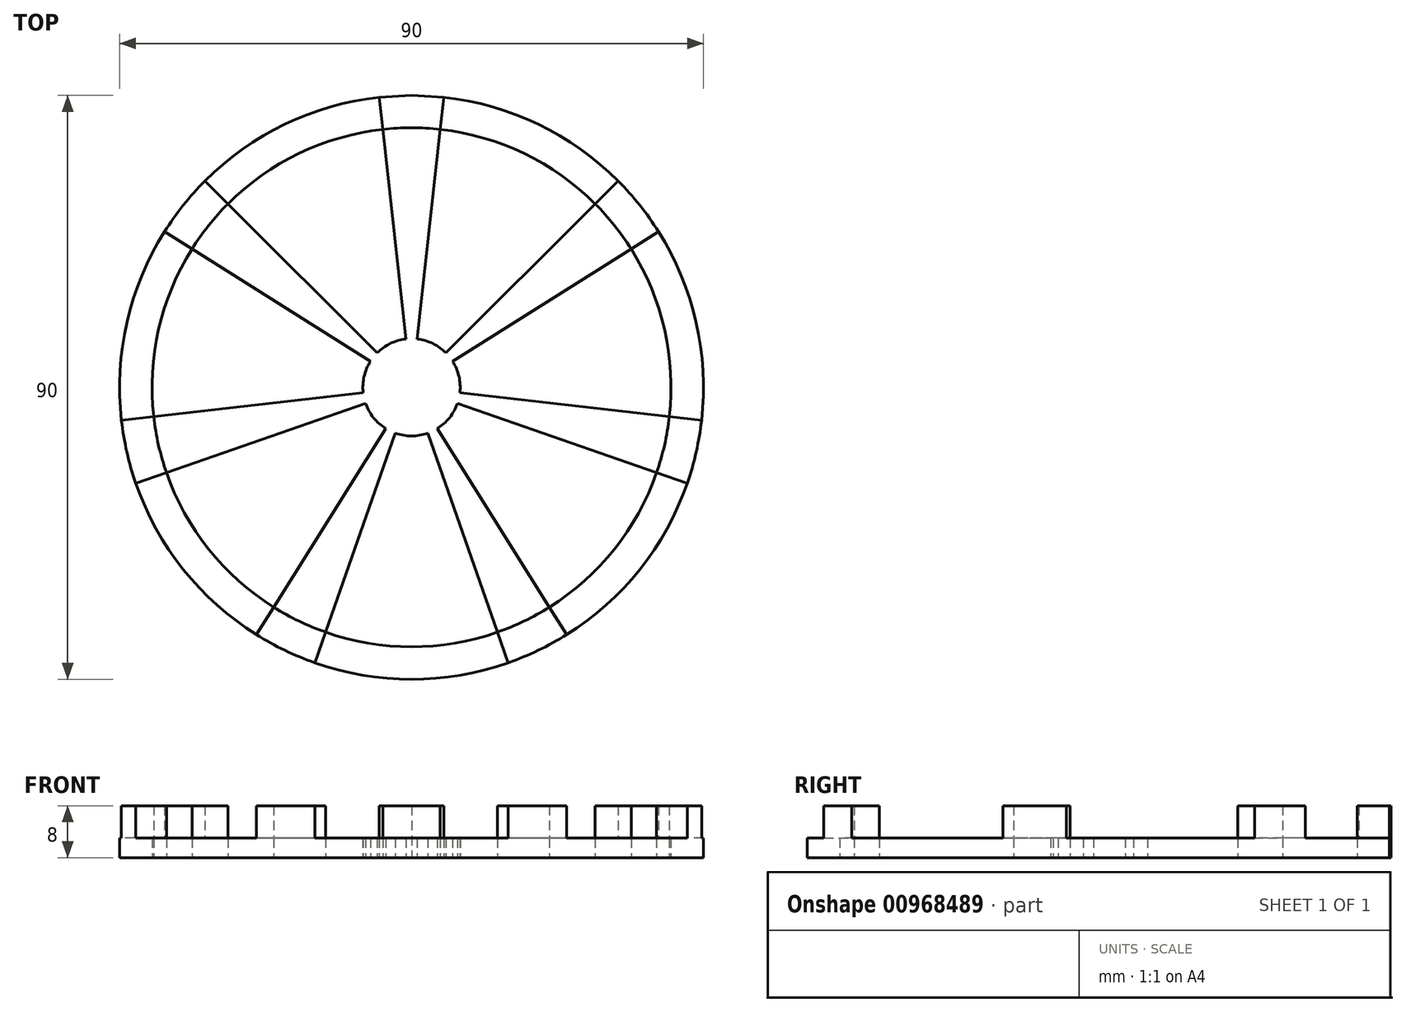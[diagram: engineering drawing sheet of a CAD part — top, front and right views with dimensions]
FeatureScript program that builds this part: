
annotation { "Feature Type Name" : "Feature", "Feature Type Description" : "" }
export const myFeature = defineFeature(function(context is Context, id is Id, definition is map)
    precondition{}
    {
        {
            var Q0;
            Q0=qCreatedBy(makeId("Top.planeOp"),FACE);
            var sketch = newSketch(context, id + "F0", { "sketchPlane" : qUnion([Q0])});
            skCircle(sketch, "E0", {"center": v(0, 0) * mm, "radius": 45 * mm});
            skCircle(sketch, "E1", {"center": v(0, 0) * mm, "radius": 7.5 * mm});
            skLineSegment(sketch, "E2", {"start": v(0, 45) * mm, "end": v(5, 44.72) * mm});
            skLineSegment(sketch, "E3.MirrorCS", {"start": v(0, 45) * mm, "end": v(-5, 44.72) * mm});
            skLineSegment(sketch, "E4", {"start": v(-5, 44.72) * mm, "end": v(0, 0) * mm});
            skLineSegment(sketch, "E5", {"start": v(0, 0) * mm, "end": v(5, 44.72) * mm});
            skLineSegment(sketch, "E6.1.0", {"start": v(0, 0) * mm, "end": v(-31.85, 31.79) * mm});
            skLineSegment(sketch, "E6.1.1", {"start": v(-38.08, 23.98) * mm, "end": v(0, 0) * mm});
            skLineSegment(sketch, "E6.2.0", {"start": v(0, 0) * mm, "end": v(-44.71, -5.08) * mm});
            skLineSegment(sketch, "E6.2.1", {"start": v(-42.5, -14.82) * mm, "end": v(0, 0) * mm});
            skLineSegment(sketch, "E6.3.0", {"start": v(0, 0) * mm, "end": v(-23.9, -38.13) * mm});
            skLineSegment(sketch, "E6.3.1", {"start": v(-14.9, -42.46) * mm, "end": v(0, 0) * mm});
            skLineSegment(sketch, "E6.4.0", {"start": v(0, 0) * mm, "end": v(14.9, -42.46) * mm});
            skLineSegment(sketch, "E6.4.1", {"start": v(23.9, -38.13) * mm, "end": v(0, 0) * mm});
            skLineSegment(sketch, "E6.5.0", {"start": v(0, 0) * mm, "end": v(42.5, -14.82) * mm});
            skLineSegment(sketch, "E6.5.1", {"start": v(44.71, -5.08) * mm, "end": v(0, 0) * mm});
            skLineSegment(sketch, "E6.6.0", {"start": v(0, 0) * mm, "end": v(38.08, 23.98) * mm});
            skLineSegment(sketch, "E6.6.1", {"start": v(31.85, 31.79) * mm, "end": v(0, 0) * mm});
            skPoint(sketch, "E7", {"position": v(-5.3, 5.3) * mm});
            skPoint(sketch, "E8", {"position": v(-0.83, 7.45) * mm});
            skPoint(sketch, "E9", {"position": v(0.83, 7.45) * mm});
            skPoint(sketch, "E10", {"position": v(5.3, 5.3) * mm});
            skPoint(sketch, "E11", {"position": v(6.35, 4) * mm});
            skPoint(sketch, "E12", {"position": v(7.45, -0.85) * mm});
            skPoint(sketch, "E13", {"position": v(7.08, -2.47) * mm});
            skPoint(sketch, "E14", {"position": v(3.98, -6.35) * mm});
            skPoint(sketch, "E15", {"position": v(2.48, -7.08) * mm});
            skPoint(sketch, "E16", {"position": v(-2.48, -7.08) * mm});
            skPoint(sketch, "E17", {"position": v(-3.98, -6.35) * mm});
            skPoint(sketch, "E18", {"position": v(-7.08, -2.47) * mm});
            skPoint(sketch, "E19", {"position": v(-7.45, -0.85) * mm});
            skPoint(sketch, "E20", {"position": v(-6.35, 4) * mm});
            skCircle(sketch, "E21.0", {"center": v(0, 0) * mm, "radius": 40 * mm});
            skSolve(sketch);
        }
        {
            var Q0;
            {var subQ1=sQuery(id+"F0.wireOp",EDGE,"E0");var subQ3=sQuery(id+"F0.wireOp",EDGE,"E6.1.0");var subQ4=makeQuery(id+"F0.imprint","INTERSECT",VERTEX,{"derivedFrom":[subQ1,subQ3]});Q0=makeQuery(id+"F0.imprint","IMPRINT",FACE,{"disambiguationData":[TD([[makeQuery(id+"F0.imprint","IMPRINT",EDGE,{"disambiguationData":[TD([[subQ4,1.0]])],"derivedFrom":subQ3}),-1.0]])]});}
            var Q1;
            {var subQ0=sQuery(id+"F0.wireOp",EDGE,"E6.1.0");var subQ1=sQuery(id+"F0.wireOp",EDGE,"E0");var subQ2=makeQuery(id+"F0.imprint","INTERSECT",VERTEX,{"derivedFrom":[subQ1,subQ0]});Q1=makeQuery(id+"F0.imprint","IMPRINT",FACE,{"disambiguationData":[TD([[makeQuery(id+"F0.imprint","IMPRINT",EDGE,{"disambiguationData":[TD([[subQ2,-1.0]])],"derivedFrom":subQ1}),1.0]])]});}
            var Q2;
            {var subQ0=sQuery(id+"F0.wireOp",EDGE,"E6.1.0");var subQ1=sQuery(id+"F0.wireOp",EDGE,"E1");var subQ2=makeQuery(id+"F0.imprint","INTERSECT",VERTEX,{"derivedFrom":[subQ1,subQ0]});Q2=makeQuery(id+"F0.imprint","IMPRINT",FACE,{"disambiguationData":[TD([[makeQuery(id+"F0.imprint","IMPRINT",EDGE,{"disambiguationData":[TD([[subQ2,-1.0]])],"derivedFrom":subQ1}),-1.0]])]});}
            var Q3;
            {var subQ0=sQuery(id+"F0.wireOp",EDGE,"E6.2.0");var subQ1=sQuery(id+"F0.wireOp",EDGE,"E1");var subQ2=makeQuery(id+"F0.imprint","INTERSECT",VERTEX,{"derivedFrom":[subQ1,subQ0]});Q3=makeQuery(id+"F0.imprint","IMPRINT",FACE,{"disambiguationData":[TD([[makeQuery(id+"F0.imprint","IMPRINT",EDGE,{"disambiguationData":[TD([[subQ2,-1.0]])],"derivedFrom":subQ1}),-1.0]])]});}
            var Q4;
            {var subQ0=sQuery(id+"F0.wireOp",EDGE,"E6.2.0");var subQ1=sQuery(id+"F0.wireOp",EDGE,"E0");var subQ2=makeQuery(id+"F0.imprint","INTERSECT",VERTEX,{"derivedFrom":[subQ1,subQ0]});Q4=makeQuery(id+"F0.imprint","IMPRINT",FACE,{"disambiguationData":[TD([[makeQuery(id+"F0.imprint","IMPRINT",EDGE,{"disambiguationData":[TD([[subQ2,-1.0]])],"derivedFrom":subQ1}),1.0]])]});}
            var Q5;
            {var subQ0=sQuery(id+"F0.wireOp",EDGE,"E6.1.1");var subQ1=sQuery(id+"F0.wireOp",EDGE,"E0");var subQ2=makeQuery(id+"F0.imprint","INTERSECT",VERTEX,{"derivedFrom":[subQ1,subQ0]});Q5=makeQuery(id+"F0.imprint","IMPRINT",FACE,{"disambiguationData":[TD([[makeQuery(id+"F0.imprint","IMPRINT",EDGE,{"disambiguationData":[TD([[subQ2,-1.0]])],"derivedFrom":subQ1}),1.0]])]});}
            var Q6;
            {var subQ0=sQuery(id+"F0.wireOp",EDGE,"E6.2.1");var subQ1=sQuery(id+"F0.wireOp",EDGE,"E0");var subQ2=makeQuery(id+"F0.imprint","INTERSECT",VERTEX,{"derivedFrom":[subQ1,subQ0]});Q6=makeQuery(id+"F0.imprint","IMPRINT",FACE,{"disambiguationData":[TD([[makeQuery(id+"F0.imprint","IMPRINT",EDGE,{"disambiguationData":[TD([[subQ2,-1.0]])],"derivedFrom":subQ1}),1.0]])]});}
            var Q7;
            {var subQ0=sQuery(id+"F0.wireOp",EDGE,"E6.3.0");var subQ1=sQuery(id+"F0.wireOp",EDGE,"E1");var subQ2=makeQuery(id+"F0.imprint","INTERSECT",VERTEX,{"derivedFrom":[subQ1,subQ0]});Q7=makeQuery(id+"F0.imprint","IMPRINT",FACE,{"disambiguationData":[TD([[makeQuery(id+"F0.imprint","IMPRINT",EDGE,{"disambiguationData":[TD([[subQ2,-1.0]])],"derivedFrom":subQ1}),-1.0]])]});}
            var Q8;
            {var subQ0=sQuery(id+"F0.wireOp",EDGE,"E6.3.0");var subQ1=sQuery(id+"F0.wireOp",EDGE,"E0");var subQ2=makeQuery(id+"F0.imprint","INTERSECT",VERTEX,{"derivedFrom":[subQ1,subQ0]});Q8=makeQuery(id+"F0.imprint","IMPRINT",FACE,{"disambiguationData":[TD([[makeQuery(id+"F0.imprint","IMPRINT",EDGE,{"disambiguationData":[TD([[subQ2,-1.0]])],"derivedFrom":subQ1}),1.0]])]});}
            var Q9;
            {var subQ0=sQuery(id+"F0.wireOp",EDGE,"E6.3.1");var subQ1=sQuery(id+"F0.wireOp",EDGE,"E0");var subQ2=makeQuery(id+"F0.imprint","INTERSECT",VERTEX,{"derivedFrom":[subQ1,subQ0]});Q9=makeQuery(id+"F0.imprint","IMPRINT",FACE,{"disambiguationData":[TD([[makeQuery(id+"F0.imprint","IMPRINT",EDGE,{"disambiguationData":[TD([[subQ2,-1.0]])],"derivedFrom":subQ1}),1.0]])]});}
            var Q10;
            {var subQ0=sQuery(id+"F0.wireOp",EDGE,"E6.4.0");var subQ1=sQuery(id+"F0.wireOp",EDGE,"E0");var subQ2=makeQuery(id+"F0.imprint","INTERSECT",VERTEX,{"derivedFrom":[subQ1,subQ0]});Q10=makeQuery(id+"F0.imprint","IMPRINT",FACE,{"disambiguationData":[TD([[makeQuery(id+"F0.imprint","IMPRINT",EDGE,{"disambiguationData":[TD([[subQ2,-1.0]])],"derivedFrom":subQ1}),1.0]])]});}
            var Q11;
            {var subQ0=sQuery(id+"F0.wireOp",EDGE,"E6.4.0");var subQ1=sQuery(id+"F0.wireOp",EDGE,"E1");var subQ2=makeQuery(id+"F0.imprint","INTERSECT",VERTEX,{"derivedFrom":[subQ1,subQ0]});Q11=makeQuery(id+"F0.imprint","IMPRINT",FACE,{"disambiguationData":[TD([[makeQuery(id+"F0.imprint","IMPRINT",EDGE,{"disambiguationData":[TD([[subQ2,-1.0]])],"derivedFrom":subQ1}),-1.0]])]});}
            var Q12;
            {var subQ0=sQuery(id+"F0.wireOp",EDGE,"E6.4.1");var subQ1=sQuery(id+"F0.wireOp",EDGE,"E0");var subQ2=makeQuery(id+"F0.imprint","INTERSECT",VERTEX,{"derivedFrom":[subQ1,subQ0]});Q12=makeQuery(id+"F0.imprint","IMPRINT",FACE,{"disambiguationData":[TD([[makeQuery(id+"F0.imprint","IMPRINT",EDGE,{"disambiguationData":[TD([[subQ2,-1.0]])],"derivedFrom":subQ1}),1.0]])]});}
            var Q13;
            {var subQ0=sQuery(id+"F0.wireOp",EDGE,"E6.5.0");var subQ1=sQuery(id+"F0.wireOp",EDGE,"E0");var subQ2=makeQuery(id+"F0.imprint","INTERSECT",VERTEX,{"derivedFrom":[subQ1,subQ0]});Q13=makeQuery(id+"F0.imprint","IMPRINT",FACE,{"disambiguationData":[TD([[makeQuery(id+"F0.imprint","IMPRINT",EDGE,{"disambiguationData":[TD([[subQ2,-1.0]])],"derivedFrom":subQ1}),1.0]])]});}
            var Q14;
            {var subQ0=sQuery(id+"F0.wireOp",EDGE,"E6.5.0");var subQ1=sQuery(id+"F0.wireOp",EDGE,"E1");var subQ2=makeQuery(id+"F0.imprint","INTERSECT",VERTEX,{"derivedFrom":[subQ1,subQ0]});Q14=makeQuery(id+"F0.imprint","IMPRINT",FACE,{"disambiguationData":[TD([[makeQuery(id+"F0.imprint","IMPRINT",EDGE,{"disambiguationData":[TD([[subQ2,-1.0]])],"derivedFrom":subQ1}),-1.0]])]});}
            var Q15;
            {var subQ0=sQuery(id+"F0.wireOp",EDGE,"E4");var subQ1=sQuery(id+"F0.wireOp",EDGE,"E1");var subQ2=makeQuery(id+"F0.imprint","INTERSECT",VERTEX,{"derivedFrom":[subQ1,subQ0]});Q15=makeQuery(id+"F0.imprint","IMPRINT",FACE,{"disambiguationData":[TD([[makeQuery(id+"F0.imprint","IMPRINT",EDGE,{"disambiguationData":[TD([[subQ2,-1.0]])],"derivedFrom":subQ1}),1.0]])]});}
            var Q16;
            {var subQ0=sQuery(id+"F0.wireOp",EDGE,"E6.1.0");var subQ1=sQuery(id+"F0.wireOp",EDGE,"E1");var subQ2=makeQuery(id+"F0.imprint","INTERSECT",VERTEX,{"derivedFrom":[subQ1,subQ0]});Q16=makeQuery(id+"F0.imprint","IMPRINT",FACE,{"disambiguationData":[TD([[makeQuery(id+"F0.imprint","IMPRINT",EDGE,{"disambiguationData":[TD([[subQ2,-1.0]])],"derivedFrom":subQ1}),1.0]])]});}
            var Q17;
            {var subQ0=sQuery(id+"F0.wireOp",EDGE,"E6.1.1");var subQ1=sQuery(id+"F0.wireOp",EDGE,"E1");var subQ2=makeQuery(id+"F0.imprint","INTERSECT",VERTEX,{"derivedFrom":[subQ1,subQ0]});Q17=makeQuery(id+"F0.imprint","IMPRINT",FACE,{"disambiguationData":[TD([[makeQuery(id+"F0.imprint","IMPRINT",EDGE,{"disambiguationData":[TD([[subQ2,-1.0]])],"derivedFrom":subQ1}),1.0]])]});}
            var Q18;
            {var subQ0=sQuery(id+"F0.wireOp",EDGE,"E6.2.0");var subQ1=sQuery(id+"F0.wireOp",EDGE,"E1");var subQ2=makeQuery(id+"F0.imprint","INTERSECT",VERTEX,{"derivedFrom":[subQ1,subQ0]});Q18=makeQuery(id+"F0.imprint","IMPRINT",FACE,{"disambiguationData":[TD([[makeQuery(id+"F0.imprint","IMPRINT",EDGE,{"disambiguationData":[TD([[subQ2,-1.0]])],"derivedFrom":subQ1}),1.0]])]});}
            var Q19;
            {var subQ0=sQuery(id+"F0.wireOp",EDGE,"E6.2.1");var subQ1=sQuery(id+"F0.wireOp",EDGE,"E1");var subQ2=makeQuery(id+"F0.imprint","INTERSECT",VERTEX,{"derivedFrom":[subQ1,subQ0]});Q19=makeQuery(id+"F0.imprint","IMPRINT",FACE,{"disambiguationData":[TD([[makeQuery(id+"F0.imprint","IMPRINT",EDGE,{"disambiguationData":[TD([[subQ2,-1.0]])],"derivedFrom":subQ1}),1.0]])]});}
            var Q20;
            {var subQ0=sQuery(id+"F0.wireOp",EDGE,"E6.3.0");var subQ1=sQuery(id+"F0.wireOp",EDGE,"E1");var subQ2=makeQuery(id+"F0.imprint","INTERSECT",VERTEX,{"derivedFrom":[subQ1,subQ0]});Q20=makeQuery(id+"F0.imprint","IMPRINT",FACE,{"disambiguationData":[TD([[makeQuery(id+"F0.imprint","IMPRINT",EDGE,{"disambiguationData":[TD([[subQ2,-1.0]])],"derivedFrom":subQ1}),1.0]])]});}
            var Q21;
            {var subQ0=sQuery(id+"F0.wireOp",EDGE,"E6.3.1");var subQ1=sQuery(id+"F0.wireOp",EDGE,"E1");var subQ2=makeQuery(id+"F0.imprint","INTERSECT",VERTEX,{"derivedFrom":[subQ1,subQ0]});Q21=makeQuery(id+"F0.imprint","IMPRINT",FACE,{"disambiguationData":[TD([[makeQuery(id+"F0.imprint","IMPRINT",EDGE,{"disambiguationData":[TD([[subQ2,-1.0]])],"derivedFrom":subQ1}),1.0]])]});}
            var Q22;
            {var subQ0=sQuery(id+"F0.wireOp",EDGE,"E6.4.0");var subQ1=sQuery(id+"F0.wireOp",EDGE,"E1");var subQ2=makeQuery(id+"F0.imprint","INTERSECT",VERTEX,{"derivedFrom":[subQ1,subQ0]});Q22=makeQuery(id+"F0.imprint","IMPRINT",FACE,{"disambiguationData":[TD([[makeQuery(id+"F0.imprint","IMPRINT",EDGE,{"disambiguationData":[TD([[subQ2,-1.0]])],"derivedFrom":subQ1}),1.0]])]});}
            var Q23;
            {var subQ0=sQuery(id+"F0.wireOp",EDGE,"E6.4.1");var subQ1=sQuery(id+"F0.wireOp",EDGE,"E1");var subQ2=makeQuery(id+"F0.imprint","INTERSECT",VERTEX,{"derivedFrom":[subQ1,subQ0]});Q23=makeQuery(id+"F0.imprint","IMPRINT",FACE,{"disambiguationData":[TD([[makeQuery(id+"F0.imprint","IMPRINT",EDGE,{"disambiguationData":[TD([[subQ2,-1.0]])],"derivedFrom":subQ1}),1.0]])]});}
            var Q24;
            {var subQ0=sQuery(id+"F0.wireOp",EDGE,"E6.5.0");var subQ1=sQuery(id+"F0.wireOp",EDGE,"E1");var subQ2=makeQuery(id+"F0.imprint","INTERSECT",VERTEX,{"derivedFrom":[subQ1,subQ0]});Q24=makeQuery(id+"F0.imprint","IMPRINT",FACE,{"disambiguationData":[TD([[makeQuery(id+"F0.imprint","IMPRINT",EDGE,{"disambiguationData":[TD([[subQ2,-1.0]])],"derivedFrom":subQ1}),1.0]])]});}
            var Q25;
            {var subQ0=sQuery(id+"F0.wireOp",EDGE,"E6.6.0");var subQ1=sQuery(id+"F0.wireOp",EDGE,"E1");var subQ2=makeQuery(id+"F0.imprint","INTERSECT",VERTEX,{"derivedFrom":[subQ1,subQ0]});Q25=makeQuery(id+"F0.imprint","IMPRINT",FACE,{"disambiguationData":[TD([[makeQuery(id+"F0.imprint","IMPRINT",EDGE,{"disambiguationData":[TD([[subQ2,1.0]])],"derivedFrom":subQ1}),1.0]])]});}
            var Q26;
            {var subQ0=sQuery(id+"F0.wireOp",EDGE,"E6.6.1");var subQ1=sQuery(id+"F0.wireOp",EDGE,"E1");var subQ2=makeQuery(id+"F0.imprint","INTERSECT",VERTEX,{"derivedFrom":[subQ1,subQ0]});Q26=makeQuery(id+"F0.imprint","IMPRINT",FACE,{"disambiguationData":[TD([[makeQuery(id+"F0.imprint","IMPRINT",EDGE,{"disambiguationData":[TD([[subQ2,1.0]])],"derivedFrom":subQ1}),1.0]])]});}
            var Q27;
            {var subQ0=sQuery(id+"F0.wireOp",EDGE,"E6.6.1");var subQ1=sQuery(id+"F0.wireOp",EDGE,"E1");var subQ2=makeQuery(id+"F0.imprint","INTERSECT",VERTEX,{"derivedFrom":[subQ1,subQ0]});Q27=makeQuery(id+"F0.imprint","IMPRINT",FACE,{"disambiguationData":[TD([[makeQuery(id+"F0.imprint","IMPRINT",EDGE,{"disambiguationData":[TD([[subQ2,-1.0]])],"derivedFrom":subQ1}),1.0]])]});}
            var Q28;
            {var subQ0=sQuery(id+"F0.wireOp",EDGE,"E5");var subQ1=sQuery(id+"F0.wireOp",EDGE,"E1");var subQ2=makeQuery(id+"F0.imprint","INTERSECT",VERTEX,{"derivedFrom":[subQ1,subQ0]});Q28=makeQuery(id+"F0.imprint","IMPRINT",FACE,{"disambiguationData":[TD([[makeQuery(id+"F0.imprint","IMPRINT",EDGE,{"disambiguationData":[TD([[subQ2,-1.0]])],"derivedFrom":subQ1}),1.0]])]});}
            var Q29;
            {var subQ0=sQuery(id+"F0.wireOp",EDGE,"E6.6.1");var subQ1=sQuery(id+"F0.wireOp",EDGE,"E1");var subQ2=makeQuery(id+"F0.imprint","INTERSECT",VERTEX,{"derivedFrom":[subQ1,subQ0]});Q29=makeQuery(id+"F0.imprint","IMPRINT",FACE,{"disambiguationData":[TD([[makeQuery(id+"F0.imprint","IMPRINT",EDGE,{"disambiguationData":[TD([[subQ2,1.0]])],"derivedFrom":subQ1}),-1.0]])]});}
            var Q30;
            {var subQ0=sQuery(id+"F0.wireOp",EDGE,"E5");var subQ1=sQuery(id+"F0.wireOp",EDGE,"E1");var subQ2=makeQuery(id+"F0.imprint","INTERSECT",VERTEX,{"derivedFrom":[subQ1,subQ0]});Q30=makeQuery(id+"F0.imprint","IMPRINT",FACE,{"disambiguationData":[TD([[makeQuery(id+"F0.imprint","IMPRINT",EDGE,{"disambiguationData":[TD([[subQ2,-1.0]])],"derivedFrom":subQ1}),-1.0]])]});}
            var Q31;
            {var subQ1=sQuery(id+"F0.wireOp",EDGE,"E2");Q31=makeQuery(id+"F0.imprint","IMPRINT",FACE,{"disambiguationData":[TD([[makeQuery(id+"F0.imprint","IMPRINT",EDGE,{"derivedFrom":subQ1}),-1.0]])]});}
            var Q32;
            {var subQ1=sQuery(id+"F0.wireOp",EDGE,"E0");var subQ3=sQuery(id+"F0.wireOp",EDGE,"E6.6.1");var subQ4=makeQuery(id+"F0.imprint","INTERSECT",VERTEX,{"derivedFrom":[subQ1,subQ3]});Q32=makeQuery(id+"F0.imprint","IMPRINT",FACE,{"disambiguationData":[TD([[makeQuery(id+"F0.imprint","IMPRINT",EDGE,{"disambiguationData":[TD([[subQ4,-1.0]])],"derivedFrom":subQ3}),-1.0]])]});}
            var Q33;
            {var subQ0=sQuery(id+"F0.wireOp",EDGE,"E6.6.0");var subQ1=sQuery(id+"F0.wireOp",EDGE,"E0");var subQ2=makeQuery(id+"F0.imprint","INTERSECT",VERTEX,{"derivedFrom":[subQ1,subQ0]});Q33=makeQuery(id+"F0.imprint","IMPRINT",FACE,{"disambiguationData":[TD([[makeQuery(id+"F0.imprint","IMPRINT",EDGE,{"disambiguationData":[TD([[subQ2,-1.0]])],"derivedFrom":subQ1}),1.0]])]});}
            var Q34;
            {var subQ0=sQuery(id+"F0.wireOp",EDGE,"E6.5.1");var subQ1=sQuery(id+"F0.wireOp",EDGE,"E0");var subQ2=makeQuery(id+"F0.imprint","INTERSECT",VERTEX,{"derivedFrom":[subQ1,subQ0]});Q34=makeQuery(id+"F0.imprint","IMPRINT",FACE,{"disambiguationData":[TD([[makeQuery(id+"F0.imprint","IMPRINT",EDGE,{"disambiguationData":[TD([[subQ2,-1.0]])],"derivedFrom":subQ1}),1.0]])]});}
            extrude(context, id + "F1", {"entities" : qUnion([Q0, Q1, Q2, Q3, Q4, Q5, Q6, Q7, Q8, Q9, Q10, Q11, Q12, Q13, Q14, Q15, Q16, Q17, Q18, Q19, Q20, Q21, Q22, Q23, Q24, Q25, Q26, Q27, Q28, Q29, Q30, Q31, Q32, Q33, Q34]), "depth" : 3 * mm, "offsetDistance" : 25 * mm});
        }
        {
            var Q0;
            {var subQ1=sQuery(id+"F0.wireOp",EDGE,"E2");Q0=makeQuery(id+"F0.imprint","IMPRINT",FACE,{"disambiguationData":[TD([[makeQuery(id+"F0.imprint","IMPRINT",EDGE,{"derivedFrom":subQ1}),-1.0]])]});}
            var Q1;
            {var subQ0=sQuery(id+"F0.wireOp",EDGE,"E6.1.0");var subQ1=sQuery(id+"F0.wireOp",EDGE,"E0");var subQ2=makeQuery(id+"F0.imprint","INTERSECT",VERTEX,{"derivedFrom":[subQ1,subQ0]});Q1=makeQuery(id+"F0.imprint","IMPRINT",FACE,{"disambiguationData":[TD([[makeQuery(id+"F0.imprint","IMPRINT",EDGE,{"disambiguationData":[TD([[subQ2,-1.0]])],"derivedFrom":subQ1}),1.0]])]});}
            var Q2;
            {var subQ0=sQuery(id+"F0.wireOp",EDGE,"E6.2.0");var subQ1=sQuery(id+"F0.wireOp",EDGE,"E0");var subQ2=makeQuery(id+"F0.imprint","INTERSECT",VERTEX,{"derivedFrom":[subQ1,subQ0]});Q2=makeQuery(id+"F0.imprint","IMPRINT",FACE,{"disambiguationData":[TD([[makeQuery(id+"F0.imprint","IMPRINT",EDGE,{"disambiguationData":[TD([[subQ2,-1.0]])],"derivedFrom":subQ1}),1.0]])]});}
            var Q3;
            {var subQ0=sQuery(id+"F0.wireOp",EDGE,"E6.3.0");var subQ1=sQuery(id+"F0.wireOp",EDGE,"E0");var subQ2=makeQuery(id+"F0.imprint","INTERSECT",VERTEX,{"derivedFrom":[subQ1,subQ0]});Q3=makeQuery(id+"F0.imprint","IMPRINT",FACE,{"disambiguationData":[TD([[makeQuery(id+"F0.imprint","IMPRINT",EDGE,{"disambiguationData":[TD([[subQ2,-1.0]])],"derivedFrom":subQ1}),1.0]])]});}
            var Q4;
            {var subQ0=sQuery(id+"F0.wireOp",EDGE,"E6.4.0");var subQ1=sQuery(id+"F0.wireOp",EDGE,"E0");var subQ2=makeQuery(id+"F0.imprint","INTERSECT",VERTEX,{"derivedFrom":[subQ1,subQ0]});Q4=makeQuery(id+"F0.imprint","IMPRINT",FACE,{"disambiguationData":[TD([[makeQuery(id+"F0.imprint","IMPRINT",EDGE,{"disambiguationData":[TD([[subQ2,-1.0]])],"derivedFrom":subQ1}),1.0]])]});}
            var Q5;
            {var subQ0=sQuery(id+"F0.wireOp",EDGE,"E6.5.0");var subQ1=sQuery(id+"F0.wireOp",EDGE,"E0");var subQ2=makeQuery(id+"F0.imprint","INTERSECT",VERTEX,{"derivedFrom":[subQ1,subQ0]});Q5=makeQuery(id+"F0.imprint","IMPRINT",FACE,{"disambiguationData":[TD([[makeQuery(id+"F0.imprint","IMPRINT",EDGE,{"disambiguationData":[TD([[subQ2,-1.0]])],"derivedFrom":subQ1}),1.0]])]});}
            var Q6;
            {var subQ0=sQuery(id+"F0.wireOp",EDGE,"E6.6.0");var subQ1=sQuery(id+"F0.wireOp",EDGE,"E0");var subQ2=makeQuery(id+"F0.imprint","INTERSECT",VERTEX,{"derivedFrom":[subQ1,subQ0]});Q6=makeQuery(id+"F0.imprint","IMPRINT",FACE,{"disambiguationData":[TD([[makeQuery(id+"F0.imprint","IMPRINT",EDGE,{"disambiguationData":[TD([[subQ2,-1.0]])],"derivedFrom":subQ1}),1.0]])]});}
            extrude(context, id + "F2", {"entities" : qUnion([Q0, Q1, Q2, Q3, Q4, Q5, Q6]), "operationType" : NewBodyOperationType.ADD, "depth" : 8 * mm, "offsetDistance" : 25 * mm});
        }
    });
